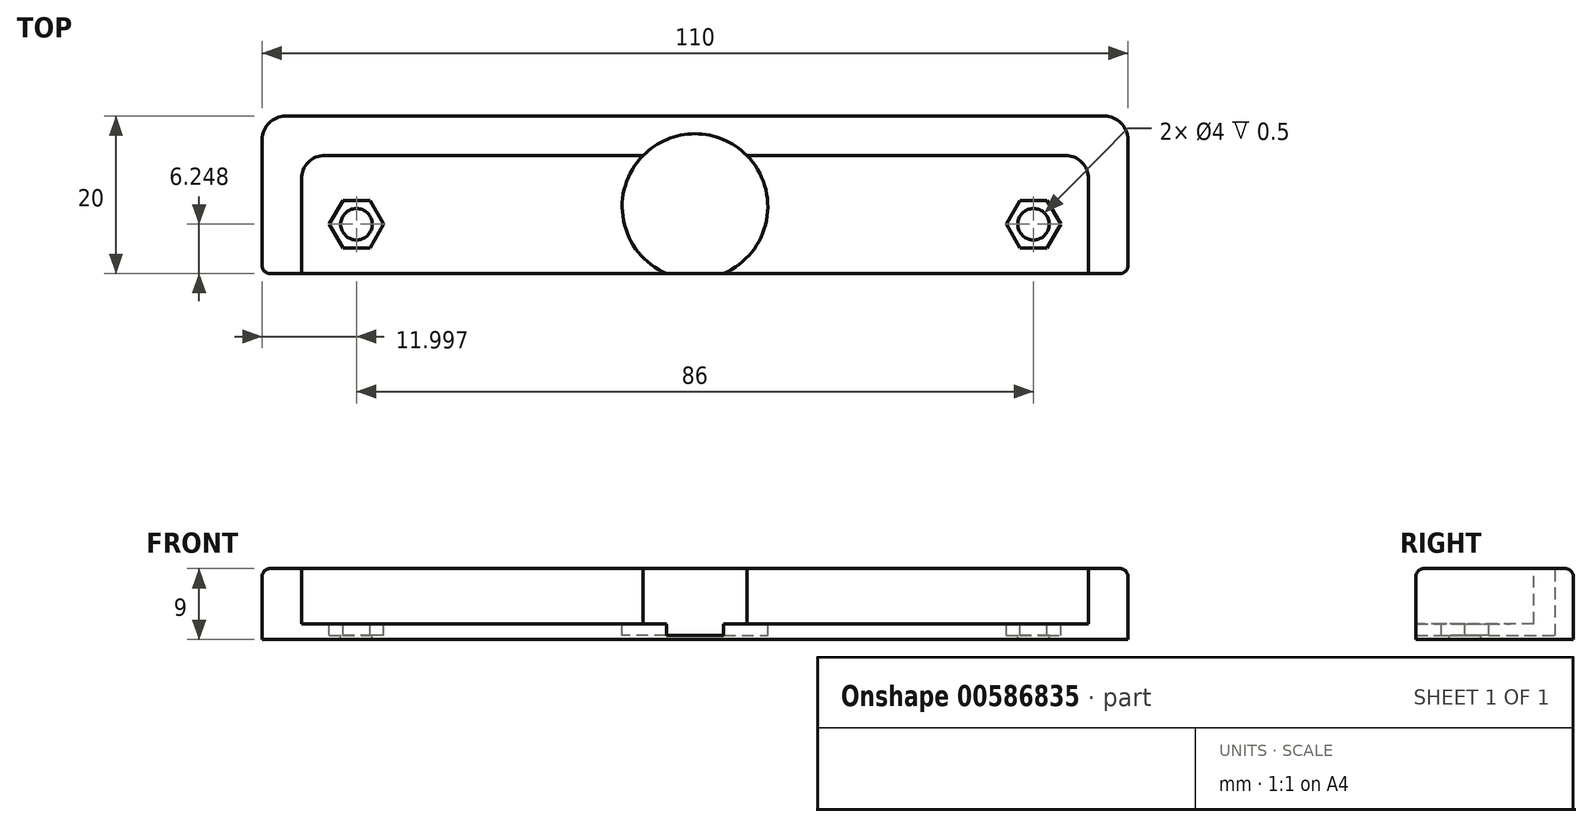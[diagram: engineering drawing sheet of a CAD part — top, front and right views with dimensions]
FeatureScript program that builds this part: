
annotation { "Feature Type Name" : "Feature", "Feature Type Description" : "" }
export const myFeature = defineFeature(function(context is Context, id is Id, definition is map)
    precondition{}
    {
        {
            var Q0;
            Q0=qCreatedBy(makeId("Top.planeOp"),FACE);
            var sketch = newSketch(context, id + "F0", { "sketchPlane" : qUnion([Q0])});
            skLineSegment(sketch, "E0.bottom", {"start": v(-48.24, -6.78) * mm, "end": v(61.76, -6.78) * mm});
            skLineSegment(sketch, "E0.top", {"start": v(-48.24, -26.78) * mm, "end": v(61.76, -26.78) * mm});
            skLineSegment(sketch, "E0.left", {"start": v(-48.24, -6.78) * mm, "end": v(-48.24, -26.78) * mm});
            skLineSegment(sketch, "E0.right", {"start": v(61.76, -6.78) * mm, "end": v(61.76, -26.78) * mm});
            skSolve(sketch);
        }
        {
            var Q0;
            Q0=qSketchRegion(id+"F0",true);
            extrude(context, id + "F1", {"entities" : qUnion([Q0]), "depth" : 9 * mm, "offsetDistance" : 25 * mm});
        }
        {
            var Q0;
            Q0=makeQuery(id+"F1.opExtrude","CAP_FACE",FACE,{"disambiguationData":[OSD([sQuery(id+"F0.wireOp",EDGE,"E0.bottom"),sQuery(id+"F0.wireOp",EDGE,"E0.top"),sQuery(id+"F0.wireOp",EDGE,"E0.left"),sQuery(id+"F0.wireOp",EDGE,"E0.right")])],"isStart":false});
            var sketch = newSketch(context, id + "F2", { "sketchPlane" : qUnion([Q0])});
            skLineSegment(sketch, "E1.bottom", {"start": v(-43.24, -26.78) * mm, "end": v(56.76, -26.78) * mm});
            skLineSegment(sketch, "E1.top", {"start": v(-43.24, -11.78) * mm, "end": v(56.76, -11.78) * mm});
            skLineSegment(sketch, "E1.left", {"start": v(-43.24, -26.78) * mm, "end": v(-43.24, -11.78) * mm});
            skLineSegment(sketch, "E1.right", {"start": v(56.76, -26.78) * mm, "end": v(56.76, -11.78) * mm});
            skSolve(sketch);
        }
        {
            var Q0;
            Q0=qSketchRegion(id+"F2",true);
            extrude(context, id + "F3", {"entities" : qUnion([Q0]), "operationType" : NewBodyOperationType.REMOVE, "oppositeDirection" : true, "depth" : 7 * mm, "offsetDistance" : 25 * mm});
        }
        {
            var Q0;
            Q0=makeQuery(id+"F3.boolean.opBoolean","COPY",EDGE,{"derivedFrom":makeQuery(id+"F3.opExtrude","SWEPT_EDGE",EDGE,{"disambiguationData":[OSD([sQuery(id+"F2.wireOp",EDGE,"E1.top"),sQuery(id+"F2.wireOp",EDGE,"E1.left")])]})});
            var Q1;
            Q1=makeQuery(id+"F3.boolean.opBoolean","COPY",EDGE,{"derivedFrom":makeQuery(id+"F3.opExtrude","SWEPT_EDGE",EDGE,{"disambiguationData":[OSD([sQuery(id+"F2.wireOp",EDGE,"E1.top"),sQuery(id+"F2.wireOp",EDGE,"E1.right")])]})});
            var Q2;
            Q2=makeQuery(id+"F1.opExtrude","SWEPT_EDGE",EDGE,{"disambiguationData":[OSD([sQuery(id+"F0.wireOp",EDGE,"E0.bottom"),sQuery(id+"F0.wireOp",EDGE,"E0.left")])]});
            var Q3;
            Q3=makeQuery(id+"F1.opExtrude","SWEPT_EDGE",EDGE,{"disambiguationData":[OSD([sQuery(id+"F0.wireOp",EDGE,"E0.bottom"),sQuery(id+"F0.wireOp",EDGE,"E0.right")])]});
            fillet(context, id + "F4", {"entities" : qUnion([Q0, Q1, Q2, Q3]), "radius" : 3 * mm, "tangentPropagation" : true, "allowEdgeOverflow" : false});
        }
        {
            var Q0;
            Q0=makeQuery(id+"F3.boolean.opBoolean","COPY",FACE,{"derivedFrom":makeQuery(id+"F3.opExtrude","CAP_FACE",FACE,{"disambiguationData":[OSD([sQuery(id+"F2.wireOp",EDGE,"E1.bottom"),sQuery(id+"F2.wireOp",EDGE,"E1.top"),sQuery(id+"F2.wireOp",EDGE,"E1.left"),sQuery(id+"F2.wireOp",EDGE,"E1.right")])],"isStart":false})});
            var sketch = newSketch(context, id + "F5", { "sketchPlane" : qUnion([Q0])});
            skCircle(sketch, "E2", {"center": v(49.76, -20.53) * mm, "radius": 2 * mm});
            skCircle(sketch, "E3", {"center": v(-36.24, -20.53) * mm, "radius": 2 * mm});
            skSolve(sketch);
        }
        {
            var Q0;
            Q0=qSketchRegion(id+"F5",true);
            extrude(context, id + "F6", {"entities" : qUnion([Q0]), "operationType" : NewBodyOperationType.REMOVE, "oppositeDirection" : true, "depth" : 20 * mm});
        }
        {
            var Q0;
            Q0=makeQuery(id+"F3.boolean.opBoolean","COPY",FACE,{"derivedFrom":makeQuery(id+"F3.opExtrude","CAP_FACE",FACE,{"disambiguationData":[OSD([sQuery(id+"F2.wireOp",EDGE,"E1.bottom"),sQuery(id+"F2.wireOp",EDGE,"E1.top"),sQuery(id+"F2.wireOp",EDGE,"E1.left"),sQuery(id+"F2.wireOp",EDGE,"E1.right")])],"isStart":false})});
            var sketch = newSketch(context, id + "F7", { "sketchPlane" : qUnion([Q0])});
            skCircle(sketch, "E4.cCircle", {"center": v(-36.24, -20.53) * mm, "radius": 3.46 * mm, "construction": true});
            skLineSegment(sketch, "E4.0", {"start": v(-37.98, -17.53) * mm, "end": v(-34.51, -17.53) * mm});
            skLineSegment(sketch, "E4.1", {"start": v(-34.51, -17.53) * mm, "end": v(-32.78, -20.53) * mm});
            skLineSegment(sketch, "E4.2", {"start": v(-32.78, -20.53) * mm, "end": v(-34.51, -23.53) * mm});
            skLineSegment(sketch, "E4.3", {"start": v(-34.51, -23.53) * mm, "end": v(-37.98, -23.53) * mm});
            skLineSegment(sketch, "E4.4", {"start": v(-37.98, -23.53) * mm, "end": v(-39.7, -20.53) * mm});
            skLineSegment(sketch, "E4.5", {"start": v(-39.7, -20.53) * mm, "end": v(-37.98, -17.53) * mm});
            skCircle(sketch, "E5.cCircle", {"center": v(49.76, -20.53) * mm, "radius": 3.46 * mm, "construction": true});
            skLineSegment(sketch, "E5.0", {"start": v(51.49, -17.53) * mm, "end": v(53.22, -20.53) * mm});
            skLineSegment(sketch, "E5.1", {"start": v(53.22, -20.53) * mm, "end": v(51.49, -23.53) * mm});
            skLineSegment(sketch, "E5.2", {"start": v(51.49, -23.53) * mm, "end": v(48.02, -23.53) * mm});
            skLineSegment(sketch, "E5.3", {"start": v(48.02, -23.53) * mm, "end": v(46.3, -20.53) * mm});
            skLineSegment(sketch, "E5.4", {"start": v(46.3, -20.53) * mm, "end": v(48.02, -17.53) * mm});
            skLineSegment(sketch, "E5.5", {"start": v(48.02, -17.53) * mm, "end": v(51.49, -17.53) * mm});
            skSolve(sketch);
        }
        {
            var Q0;
            Q0 = qSketchRegion(id + "F7", true);
            extrude(context, id + "F8", {"entities" : qUnion([Q0]), "operationType" : NewBodyOperationType.REMOVE, "oppositeDirection" : true, "depth" : 1.5 * mm, "offsetDistance" : 25 * mm});
        }
        {
            var Q0;
            Q0=makeQuery(id+"F3.boolean.opBoolean","COPY",FACE,{"derivedFrom":makeQuery(id+"F3.opExtrude","CAP_FACE",FACE,{"disambiguationData":[OSD([sQuery(id+"F2.wireOp",EDGE,"E1.bottom"),sQuery(id+"F2.wireOp",EDGE,"E1.top"),sQuery(id+"F2.wireOp",EDGE,"E1.left"),sQuery(id+"F2.wireOp",EDGE,"E1.right")])],"isStart":false})});
            var sketch = newSketch(context, id + "F9", { "sketchPlane" : qUnion([Q0])});
            skCircle(sketch, "E6", {"center": v(6.76, -18.28) * mm, "radius": 9.25 * mm});
            skSolve(sketch);
        }
        {
            var Q0;
            Q0=qSketchRegion(id+"F9",true);
            extrude(context, id + "F10", {"entities" : qUnion([Q0]), "operationType" : NewBodyOperationType.REMOVE, "oppositeDirection" : true, "depth" : 1.5 * mm, "hasSecondDirection" : true, "secondDirectionOppositeDirection" : false, "secondDirectionDepth" : 7 * mm, "offsetDistance" : 25 * mm});
        }
        {
            var Q0;
            Q0=makeQuery(id+"F1.opExtrude","CAP_EDGE",EDGE,{"disambiguationData":[OSD([sQuery(id+"F0.wireOp",EDGE,"E0.bottom")])],"isStart":false});
            var Q1;
            Q1=makeQuery(id+"F1.opExtrude","SWEPT_EDGE",EDGE,{"disambiguationData":[OSD([sQuery(id+"F0.wireOp",EDGE,"E0.top"),sQuery(id+"F0.wireOp",EDGE,"E0.left")])]});
            var Q2;
            Q2=makeQuery(id+"F1.opExtrude","SWEPT_EDGE",EDGE,{"disambiguationData":[OSD([sQuery(id+"F0.wireOp",EDGE,"E0.top"),sQuery(id+"F0.wireOp",EDGE,"E0.right")])]});
            var Q3;
            {var subQ0=sQuery(id+"F0.wireOp",EDGE,"E0.right");var subQ1=sQuery(id+"F0.wireOp",EDGE,"E0.top");Q3=makeQuery(id+"F3.boolean.opBoolean","SPLIT",EDGE,{"disambiguationData":[TD([makeQuery(id+"F1.opExtrude","SWEPT_FACE",FACE,{"disambiguationData":[OSD([subQ0])]})])],"derivedFrom":makeQuery(id+"F1.opExtrude","CAP_EDGE",EDGE,{"disambiguationData":[OSD([subQ1])],"isStart":false})});}
            var Q4;
            {var subQ0=sQuery(id+"F0.wireOp",EDGE,"E0.left");var subQ1=sQuery(id+"F0.wireOp",EDGE,"E0.top");Q4=makeQuery(id+"F3.boolean.opBoolean","SPLIT",EDGE,{"disambiguationData":[TD([makeQuery(id+"F1.opExtrude","SWEPT_FACE",FACE,{"disambiguationData":[OSD([subQ0])]})])],"derivedFrom":makeQuery(id+"F1.opExtrude","CAP_EDGE",EDGE,{"disambiguationData":[OSD([subQ1])],"isStart":false})});}
            fillet(context, id + "F11", {"entities" : qUnion([Q0, Q1, Q2, Q3, Q4]), "radius" : 1 * mm, "tangentPropagation" : true, "allowEdgeOverflow" : false});
        }
    });
